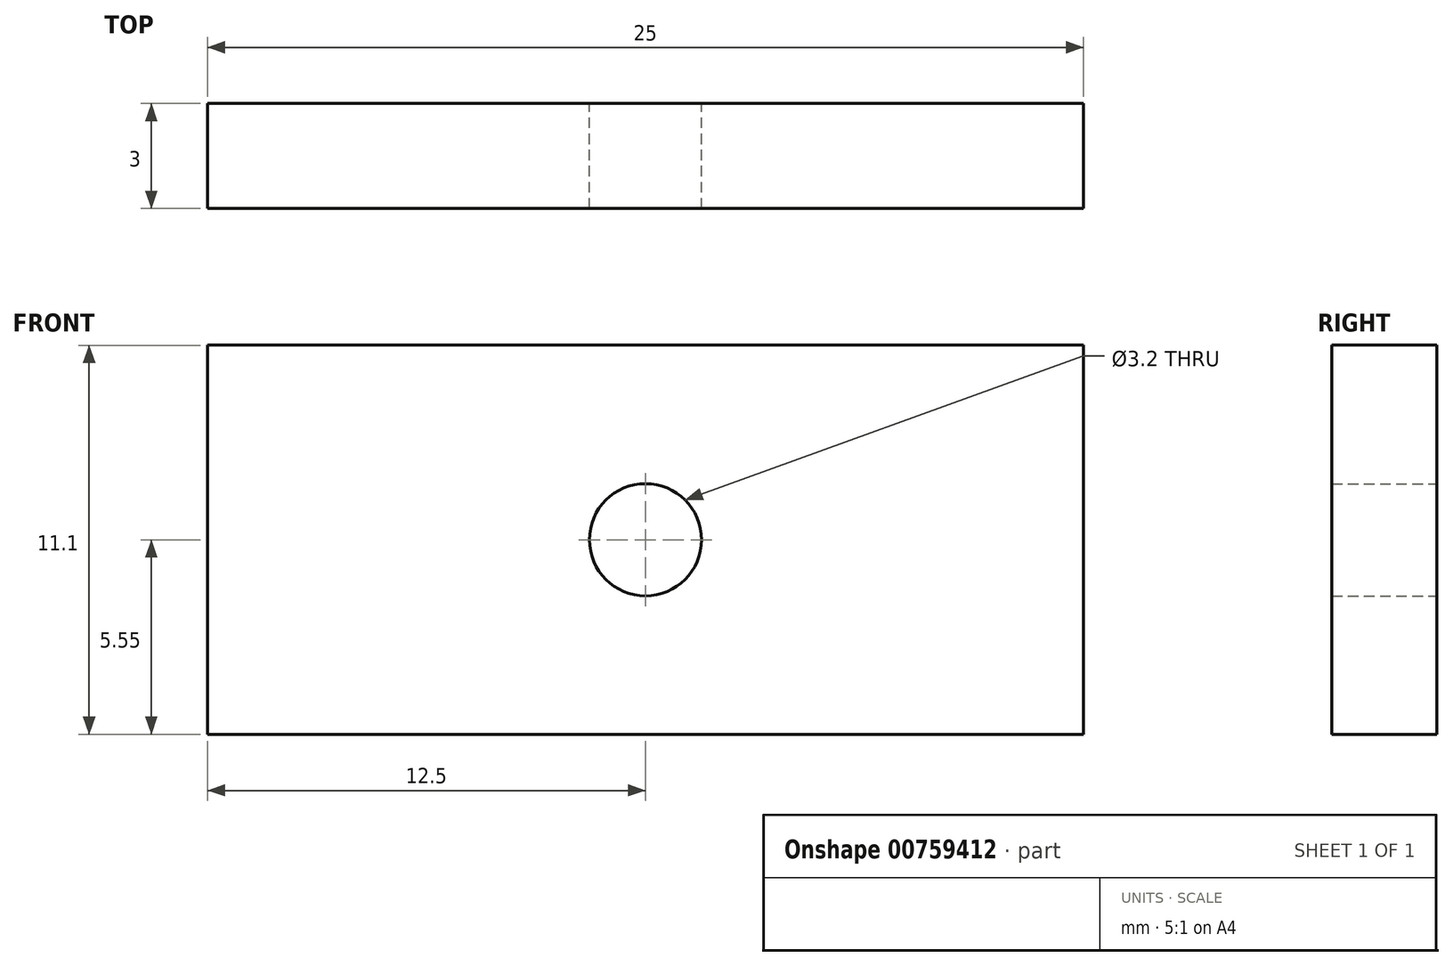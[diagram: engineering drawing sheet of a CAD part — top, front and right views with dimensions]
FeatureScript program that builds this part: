
annotation { "Feature Type Name" : "Feature", "Feature Type Description" : "" }
export const myFeature = defineFeature(function(context is Context, id is Id, definition is map)
    precondition{}
    {
        {
            var Q0;
            Q0=qCreatedBy(makeId("Front.planeOp"),FACE);
            var sketch = newSketch(context, id + "F0", { "sketchPlane" : qUnion([Q0])});
            skLineSegment(sketch, "E0.bottom", {"start": v(12.5, -5.55) * mm, "end": v(-12.5, -5.55) * mm});
            skLineSegment(sketch, "E0.top", {"start": v(12.5, 5.56) * mm, "end": v(-12.5, 5.55) * mm});
            skLineSegment(sketch, "E0.left", {"start": v(12.5, -5.55) * mm, "end": v(12.5, 5.56) * mm});
            skLineSegment(sketch, "E0.right", {"start": v(-12.5, -5.56) * mm, "end": v(-12.5, 5.56) * mm});
            skPoint(sketch, "E0.middle", {"position": v(0, 0) * mm});
            skCircle(sketch, "E1", {"center": v(0, 0) * mm, "radius": 1.6 * mm});
            skSolve(sketch);
        }
        {
            var Q0;
            Q0 = qSketchRegion(id + "F0", true);
            extrude(context, id + "F1", {"entities" : qUnion([Q0]), "depth" : 3 * mm, "offsetDistance" : 25 * mm});
        }
    });
